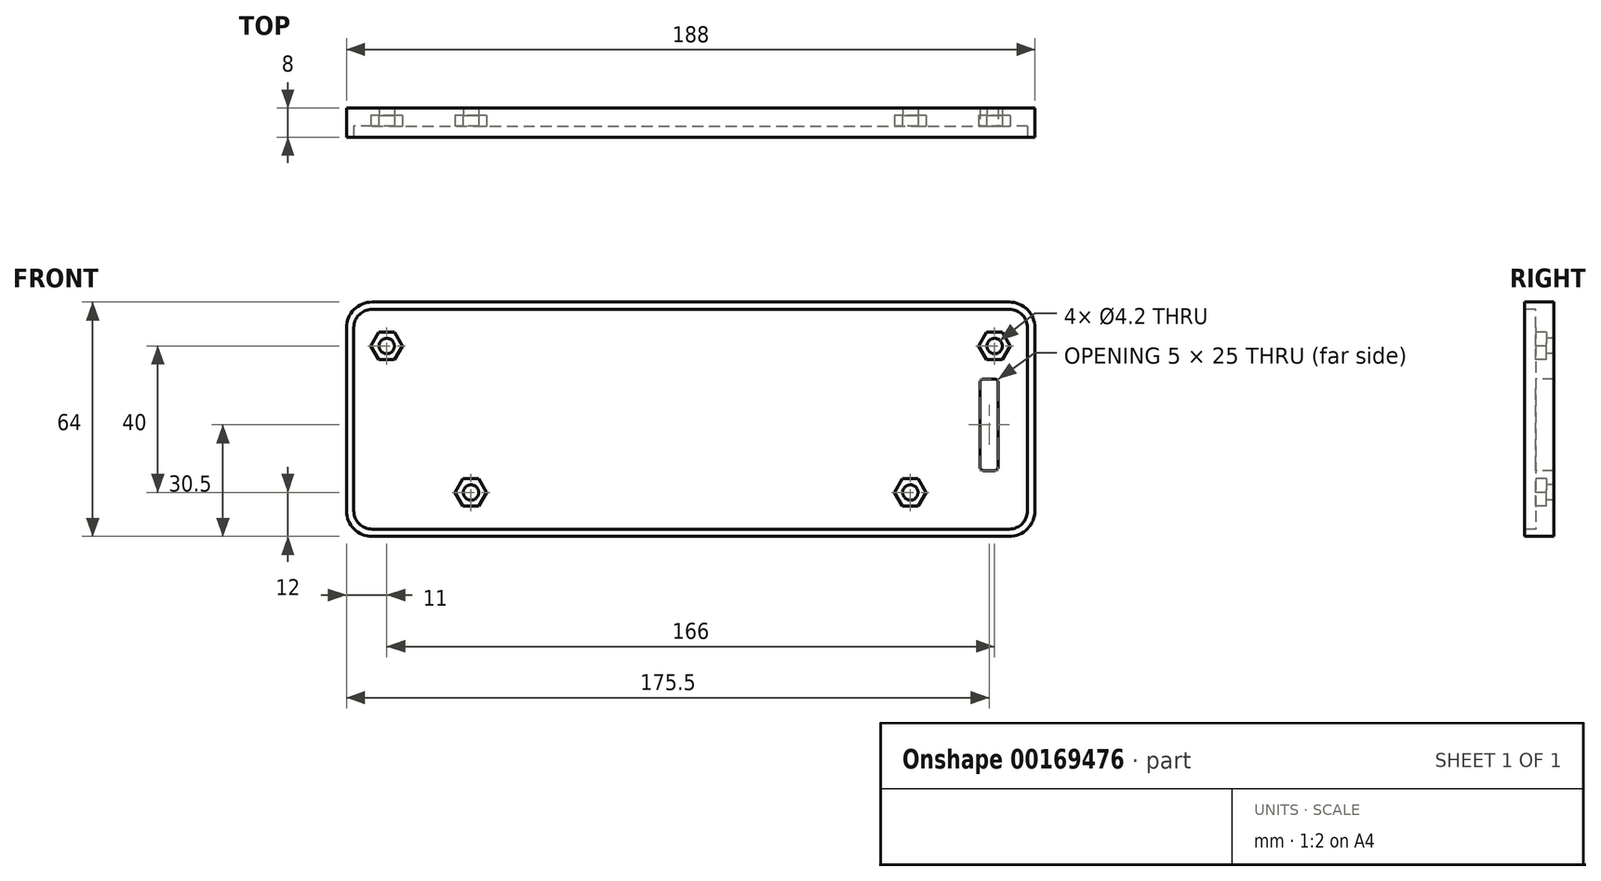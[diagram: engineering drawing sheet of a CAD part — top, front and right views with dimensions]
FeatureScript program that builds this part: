
annotation { "Feature Type Name" : "Feature", "Feature Type Description" : "" }
export const myFeature = defineFeature(function(context is Context, id is Id, definition is map)
    precondition{}
    {
        {
            var Q0;
            Q0=qCreatedBy(makeId("Front.planeOp"),FACE);
            var sketch = newSketch(context, id + "F0", { "sketchPlane" : qUnion([Q0])});
            skLineSegment(sketch, "E0.bottom", {"start": v(87, -32) * mm, "end": v(-87, -32) * mm});
            skLineSegment(sketch, "E0.top", {"start": v(87, 32) * mm, "end": v(-87, 32) * mm});
            skLineSegment(sketch, "E0.left", {"start": v(94, -25) * mm, "end": v(94, 25) * mm});
            skLineSegment(sketch, "E0.right", {"start": v(-94, -25) * mm, "end": v(-94, 25) * mm});
            skPoint(sketch, "E0.middle", {"position": v(0, 0) * mm});
            skPoint(sketch, "E1.visualSharp", {"position": v(-94, 32) * mm});
            skArc(sketch, "E1.filletArc", {"start": v(-87, 32) * mm, "mid": v(-91.95, 29.95) * mm, "end": v(-94, 25) * mm});
            skPoint(sketch, "E2.visualSharp", {"position": v(94, 32) * mm});
            skArc(sketch, "E2.filletArc", {"start": v(94, 25) * mm, "mid": v(91.95, 29.95) * mm, "end": v(87, 32) * mm});
            skPoint(sketch, "E3.visualSharp", {"position": v(94, -32) * mm});
            skArc(sketch, "E3.filletArc", {"start": v(87, -32) * mm, "mid": v(91.95, -29.95) * mm, "end": v(94, -25) * mm});
            skPoint(sketch, "E4.visualSharp", {"position": v(-94, -32) * mm});
            skArc(sketch, "E4.filletArc", {"start": v(-94, -25) * mm, "mid": v(-91.95, -29.95) * mm, "end": v(-87, -32) * mm});
            skSolve(sketch);
        }
        {
            var Q0;
            Q0 = qSketchRegion(id + "F0", true);
            extrude(context, id + "F1", {"entities" : qUnion([Q0]), "depth" : 8 * mm});
        }
        {
            var Q0;
            Q0=makeQuery(id+"F1.opExtrude","CAP_FACE",FACE,{"disambiguationData":[OSD([sQuery(id+"F0.wireOp",EDGE,"E0.bottom"),sQuery(id+"F0.wireOp",EDGE,"E0.top"),sQuery(id+"F0.wireOp",EDGE,"E0.left"),sQuery(id+"F0.wireOp",EDGE,"E0.right"),sQuery(id+"F0.wireOp",EDGE,"E1.filletArc"),sQuery(id+"F0.wireOp",EDGE,"E2.filletArc"),sQuery(id+"F0.wireOp",EDGE,"E3.filletArc"),sQuery(id+"F0.wireOp",EDGE,"E4.filletArc")])],"isStart":false});
            var sketch = newSketch(context, id + "F2", { "sketchPlane" : qUnion([Q0])});
            skLineSegment(sketch, "E5.bottom", {"start": v(-87, 30) * mm, "end": v(87, 30) * mm});
            skLineSegment(sketch, "E5.top", {"start": v(-87, -30) * mm, "end": v(87, -30) * mm});
            skLineSegment(sketch, "E5.left", {"start": v(-92, 25) * mm, "end": v(-92, -25) * mm});
            skLineSegment(sketch, "E5.right", {"start": v(92, 25) * mm, "end": v(92, -25) * mm});
            skPoint(sketch, "E6.visualSharp", {"position": v(-92, 30) * mm});
            skArc(sketch, "E6.filletArc", {"start": v(-87, 30) * mm, "mid": v(-90.54, 28.54) * mm, "end": v(-92, 25) * mm});
            skPoint(sketch, "E7.visualSharp", {"position": v(92, 30) * mm});
            skArc(sketch, "E7.filletArc", {"start": v(92, 25) * mm, "mid": v(90.54, 28.54) * mm, "end": v(87, 30) * mm});
            skPoint(sketch, "E8.visualSharp", {"position": v(92, -30) * mm});
            skArc(sketch, "E8.filletArc", {"start": v(87, -30) * mm, "mid": v(90.54, -28.54) * mm, "end": v(92, -25) * mm});
            skPoint(sketch, "E9.visualSharp", {"position": v(-92, -30) * mm});
            skArc(sketch, "E9.filletArc", {"start": v(-92, -25) * mm, "mid": v(-90.54, -28.54) * mm, "end": v(-87, -30) * mm});
            skSolve(sketch);
        }
        {
            var Q0;
            Q0 = qSketchRegion(id + "F2", true);
            extrude(context, id + "F3", {"entities" : qUnion([Q0]), "operationType" : NewBodyOperationType.REMOVE, "oppositeDirection" : true, "depth" : 3 * mm});
        }
        {
            var Q0;
            Q0=makeQuery(id+"F0.imprint","IMPRINT",FACE,{"disambiguationData":[TD([[makeQuery(id+"F0.imprint","IMPRINT",EDGE,{"derivedFrom":sQuery(id+"F0.wireOp",EDGE,"E0.bottom")}),-1.0]])]});
            var sketch = newSketch(context, id + "F4", { "sketchPlane" : qUnion([Q0])});
            skLineSegment(sketch, "E10.bottom", {"start": v(-87, 30) * mm, "end": v(87, 30) * mm});
            skLineSegment(sketch, "E10.top", {"start": v(-87, -30) * mm, "end": v(87, -30) * mm});
            skLineSegment(sketch, "E10.left", {"start": v(-92, 25) * mm, "end": v(-92, -25) * mm});
            skLineSegment(sketch, "E10.right", {"start": v(92, 25) * mm, "end": v(92, -25) * mm});
            skPoint(sketch, "E11.visualSharp", {"position": v(92, -30) * mm});
            skPoint(sketch, "E12.visualSharp", {"position": v(-92, -30) * mm});
            skPoint(sketch, "E13.visualSharp", {"position": v(-92, 30) * mm});
            skPoint(sketch, "E14.visualSharp", {"position": v(92, 30) * mm});
            skArc(sketch, "E15.filletArc", {"start": v(-87, 30) * mm, "mid": v(-90.54, 28.54) * mm, "end": v(-92, 25) * mm});
            skArc(sketch, "E16.filletArc", {"start": v(-92, -25) * mm, "mid": v(-90.54, -28.54) * mm, "end": v(-87, -30) * mm});
            skArc(sketch, "E17.filletArc", {"start": v(92, 25) * mm, "mid": v(90.54, 28.54) * mm, "end": v(87, 30) * mm});
            skArc(sketch, "E18.filletArc", {"start": v(87, -30) * mm, "mid": v(90.54, -28.54) * mm, "end": v(92, -25) * mm});
            skSolve(sketch);
        }
        {
            var Q0;
            Q0=makeQuery(id+"F3.boolean.opBoolean","COPY",FACE,{"derivedFrom":makeQuery(id+"F3.opExtrude","CAP_FACE",FACE,{"disambiguationData":[OSD([sQuery(id+"F2.wireOp",EDGE,"E5.bottom"),sQuery(id+"F2.wireOp",EDGE,"E5.top"),sQuery(id+"F2.wireOp",EDGE,"E5.left"),sQuery(id+"F2.wireOp",EDGE,"E5.right"),sQuery(id+"F2.wireOp",EDGE,"E6.filletArc"),sQuery(id+"F2.wireOp",EDGE,"E7.filletArc"),sQuery(id+"F2.wireOp",EDGE,"E8.filletArc"),sQuery(id+"F2.wireOp",EDGE,"E9.filletArc")])],"isStart":false})});
            var sketch = newSketch(context, id + "F5", { "sketchPlane" : qUnion([Q0])});
            skLineSegment(sketch, "E19", {"start": v(-92, 0) * mm, "end": v(92, 0) * mm, "construction": true});
            skLineSegment(sketch, "E20", {"start": v(0, 30) * mm, "end": v(0, -30) * mm, "construction": true});
            skSolve(sketch);
        }
        {
            var Q0;
            Q0=makeQuery(id+"F5.imprint","IMPRINT",FACE,{"disambiguationData":[TD([[makeQuery(id+"F5.imprint","IMPRINT",EDGE,{"derivedFrom":makeQuery(id+"F3.boolean.opBoolean","COPY",EDGE,{"derivedFrom":makeQuery(id+"F3.opExtrude","CAP_EDGE",EDGE,{"disambiguationData":[OSD([sQuery(id+"F2.wireOp",EDGE,"E5.bottom")])],"isStart":false})})}),-1.0]])]});
            var sketch = newSketch(context, id + "F6", { "sketchPlane" : qUnion([Q0])});
            skCircle(sketch, "E21.cCircle", {"center": v(60, -20) * mm, "radius": 3.75 * mm, "construction": true});
            skLineSegment(sketch, "E21.0", {"start": v(57.83, -23.75) * mm, "end": v(55.67, -20) * mm});
            skLineSegment(sketch, "E21.1", {"start": v(55.67, -20) * mm, "end": v(57.83, -16.25) * mm});
            skLineSegment(sketch, "E21.2", {"start": v(57.83, -16.25) * mm, "end": v(62.17, -16.25) * mm});
            skLineSegment(sketch, "E21.3", {"start": v(62.17, -16.25) * mm, "end": v(64.33, -20) * mm});
            skLineSegment(sketch, "E21.4", {"start": v(64.33, -20) * mm, "end": v(62.17, -23.75) * mm});
            skLineSegment(sketch, "E21.5", {"start": v(62.17, -23.75) * mm, "end": v(57.83, -23.75) * mm});
            skPoint(sketch, "E21.0.midPoint", {"position": v(56.75, -21.88) * mm});
            skCircle(sketch, "E22.cCircle", {"center": v(83, 20) * mm, "radius": 3.75 * mm, "construction": true});
            skLineSegment(sketch, "E22.0", {"start": v(80.83, 16.25) * mm, "end": v(78.67, 20) * mm});
            skLineSegment(sketch, "E22.1", {"start": v(78.67, 20) * mm, "end": v(80.83, 23.75) * mm});
            skLineSegment(sketch, "E22.2", {"start": v(80.83, 23.75) * mm, "end": v(85.17, 23.75) * mm});
            skLineSegment(sketch, "E22.3", {"start": v(85.17, 23.75) * mm, "end": v(87.33, 20) * mm});
            skLineSegment(sketch, "E22.4", {"start": v(87.33, 20) * mm, "end": v(85.17, 16.25) * mm});
            skLineSegment(sketch, "E22.5", {"start": v(85.17, 16.25) * mm, "end": v(80.83, 16.25) * mm});
            skPoint(sketch, "E22.0.midPoint", {"position": v(79.75, 18.12) * mm});
            skCircle(sketch, "E23.cCircle", {"center": v(-60, -20) * mm, "radius": 3.75 * mm, "construction": true});
            skLineSegment(sketch, "E23.0", {"start": v(-62.17, -23.75) * mm, "end": v(-64.33, -20) * mm});
            skLineSegment(sketch, "E23.1", {"start": v(-64.33, -20) * mm, "end": v(-62.17, -16.25) * mm});
            skLineSegment(sketch, "E23.2", {"start": v(-62.17, -16.25) * mm, "end": v(-57.83, -16.25) * mm});
            skLineSegment(sketch, "E23.3", {"start": v(-57.83, -16.25) * mm, "end": v(-55.67, -20) * mm});
            skLineSegment(sketch, "E23.4", {"start": v(-55.67, -20) * mm, "end": v(-57.83, -23.75) * mm});
            skLineSegment(sketch, "E23.5", {"start": v(-57.83, -23.75) * mm, "end": v(-62.17, -23.75) * mm});
            skPoint(sketch, "E23.0.midPoint", {"position": v(-63.75, -20) * mm});
            skCircle(sketch, "E24.cCircle", {"center": v(-83, 20) * mm, "radius": 3.75 * mm, "construction": true});
            skLineSegment(sketch, "E24.0", {"start": v(-85.17, 16.25) * mm, "end": v(-87.33, 20) * mm});
            skLineSegment(sketch, "E24.1", {"start": v(-87.33, 20) * mm, "end": v(-85.17, 23.75) * mm});
            skLineSegment(sketch, "E24.2", {"start": v(-85.17, 23.75) * mm, "end": v(-80.83, 23.75) * mm});
            skLineSegment(sketch, "E24.3", {"start": v(-80.83, 23.75) * mm, "end": v(-78.67, 20) * mm});
            skLineSegment(sketch, "E24.4", {"start": v(-78.67, 20) * mm, "end": v(-80.83, 16.25) * mm});
            skLineSegment(sketch, "E24.5", {"start": v(-80.83, 16.25) * mm, "end": v(-85.17, 16.25) * mm});
            skPoint(sketch, "E24.0.midPoint", {"position": v(-86.25, 18.13) * mm});
            skSolve(sketch);
        }
        {
            var Q0;
            Q0 = qSketchRegion(id + "F6", true);
            extrude(context, id + "F7", {"entities" : qUnion([Q0]), "operationType" : NewBodyOperationType.REMOVE, "oppositeDirection" : true, "depth" : 3 * mm});
        }
        {
            var Q0;
            Q0=makeQuery(id+"F5.imprint","IMPRINT",FACE,{"disambiguationData":[TD([[makeQuery(id+"F5.imprint","IMPRINT",EDGE,{"derivedFrom":makeQuery(id+"F3.boolean.opBoolean","COPY",EDGE,{"derivedFrom":makeQuery(id+"F3.opExtrude","CAP_EDGE",EDGE,{"disambiguationData":[OSD([sQuery(id+"F2.wireOp",EDGE,"E5.bottom")])],"isStart":false})})}),-1.0]])]});
            var sketch = newSketch(context, id + "F8", { "sketchPlane" : qUnion([Q0])});
            skCircle(sketch, "E25", {"center": v(-83, 20) * mm, "radius": 2.1 * mm});
            skCircle(sketch, "E26", {"center": v(-60, -20) * mm, "radius": 2.1 * mm});
            skCircle(sketch, "E27", {"center": v(83, 20) * mm, "radius": 2.1 * mm});
            skCircle(sketch, "E28", {"center": v(60, -20) * mm, "radius": 2.1 * mm});
            skSolve(sketch);
        }
        {
            var Q0;
            Q0 = qSketchRegion(id + "F8", true);
            var Q1;
            Q1=makeQuery(id+"F1.opExtrude","CAP_FACE",FACE,{"disambiguationData":[OSD([sQuery(id+"F0.wireOp",EDGE,"E0.bottom"),sQuery(id+"F0.wireOp",EDGE,"E0.top"),sQuery(id+"F0.wireOp",EDGE,"E0.left"),sQuery(id+"F0.wireOp",EDGE,"E0.right"),sQuery(id+"F0.wireOp",EDGE,"E1.filletArc"),sQuery(id+"F0.wireOp",EDGE,"E2.filletArc"),sQuery(id+"F0.wireOp",EDGE,"E3.filletArc"),sQuery(id+"F0.wireOp",EDGE,"E4.filletArc")])],"isStart":true});
            extrude(context, id + "F9", {"entities" : qUnion([Q0]), "operationType" : NewBodyOperationType.REMOVE, "endBound" : BoundingType.UP_TO_SURFACE, "oppositeDirection" : true, "endBoundEntityFace" : qUnion([Q1]), "depth" : 25 * mm});
        }
        {
            var Q0;
            Q0=makeQuery(id+"F3.boolean.opBoolean","COPY",FACE,{"derivedFrom":makeQuery(id+"F3.opExtrude","SWEPT_FACE",FACE,{"disambiguationData":[OSD([sQuery(id+"F2.wireOp",EDGE,"E5.left")])]})});
            var sketch = newSketch(context, id + "F10", { "sketchPlane" : qUnion([Q0])});
            skLineSegment(sketch, "E29.bottom", {"start": v(-6.2, -10) * mm, "end": v(-5, -10) * mm});
            skLineSegment(sketch, "E29.top", {"start": v(-6.2, -21) * mm, "end": v(-5, -21) * mm});
            skLineSegment(sketch, "E29.left", {"start": v(-6.2, -10) * mm, "end": v(-6.2, -21) * mm});
            skLineSegment(sketch, "E29.right", {"start": v(-5, -10) * mm, "end": v(-5, -21) * mm});
            skLineSegment(sketch, "E30.bottom", {"start": v(-6.2, 21) * mm, "end": v(-5, 21) * mm});
            skLineSegment(sketch, "E30.top", {"start": v(-6.2, 10) * mm, "end": v(-5, 10) * mm});
            skLineSegment(sketch, "E30.left", {"start": v(-6.2, 21) * mm, "end": v(-6.2, 10) * mm});
            skLineSegment(sketch, "E30.right", {"start": v(-5, 21) * mm, "end": v(-5, 10) * mm});
            skSolve(sketch);
        }
        {
            var Q0;
            Q0=makeQuery(id+"F3.boolean.opBoolean","COPY",FACE,{"derivedFrom":makeQuery(id+"F3.opExtrude","SWEPT_FACE",FACE,{"disambiguationData":[OSD([sQuery(id+"F2.wireOp",EDGE,"E5.right")])]})});
            var sketch = newSketch(context, id + "F11", { "sketchPlane" : qUnion([Q0])});
            skLineSegment(sketch, "E31.bottom", {"start": v(5, 21) * mm, "end": v(6.2, 21) * mm});
            skLineSegment(sketch, "E31.top", {"start": v(5, 10) * mm, "end": v(6.2, 10) * mm});
            skLineSegment(sketch, "E31.left", {"start": v(5, 21) * mm, "end": v(5, 10) * mm});
            skLineSegment(sketch, "E31.right", {"start": v(6.2, 21) * mm, "end": v(6.2, 10) * mm});
            skLineSegment(sketch, "E32.bottom", {"start": v(5, -21) * mm, "end": v(6.2, -21) * mm});
            skLineSegment(sketch, "E32.top", {"start": v(5, -10) * mm, "end": v(6.2, -10) * mm});
            skLineSegment(sketch, "E32.left", {"start": v(5, -10) * mm, "end": v(5, -21) * mm});
            skLineSegment(sketch, "E32.right", {"start": v(6.2, -10) * mm, "end": v(6.2, -21) * mm});
            skSolve(sketch);
        }
        {
            var Q0;
            Q0=makeQuery(id+"FXRFE9z9mOGoDKD_1.boolean.opBoolean","MERGE",FACE,{"derivedFrom":[makeQuery(id+"FHSEXAi1wgHX63n_1.boolean.opBoolean","MERGE",FACE,{"derivedFrom":[makeQuery(id+"FVbHBnZoGS1GzSc_1.boolean.opBoolean","MERGE",FACE,{"derivedFrom":[makeQuery(id+"F3.boolean.opBoolean","COPY",FACE,{"derivedFrom":makeQuery(id+"F3.opExtrude","CAP_FACE",FACE,{"disambiguationData":[OSD([sQuery(id+"F2.wireOp",EDGE,"E5.bottom"),sQuery(id+"F2.wireOp",EDGE,"E5.top"),sQuery(id+"F2.wireOp",EDGE,"E5.left"),sQuery(id+"F2.wireOp",EDGE,"E5.right"),sQuery(id+"F2.wireOp",EDGE,"E6.filletArc"),sQuery(id+"F2.wireOp",EDGE,"E7.filletArc"),sQuery(id+"F2.wireOp",EDGE,"E8.filletArc"),sQuery(id+"F2.wireOp",EDGE,"E9.filletArc")])],"isStart":false})}),makeQuery(id+"FVbHBnZoGS1GzSc_1.opExtrude","SWEPT_FACE",FACE,{"disambiguationData":[OSD([sQuery(id+"F10.wireOp",EDGE,"f3jfxRYR-zEYV-4sXy-QslR-nipfOOar7KBW")])]})]}),makeQuery(id+"FHSEXAi1wgHX63n_1.opExtrude","SWEPT_FACE",FACE,{"disambiguationData":[OSD([sQuery(id+"F11.wireOp",EDGE,"W6rOKNuU-GTvi-akX3-pjKq-6DrbPIyYzJpk"),sQuery(id+"F11.wireOp",EDGE,"2wJdlAmh-kTGb-LktZ-zVvI-ko3Y32ltAbLw")])]})]}),makeQuery(id+"FXRFE9z9mOGoDKD_1.opExtrude","SWEPT_FACE",FACE,{"disambiguationData":[OSD([sQuery(id+"FBFUB2NdTQuH0OG_1.wireOp",EDGE,"6aijx3dq-d6Lm-KUiO-0isF-x3RtKitpbzHq.left")])]}),makeQuery(id+"FXRFE9z9mOGoDKD_1.opExtrude","SWEPT_FACE",FACE,{"disambiguationData":[OSD([sQuery(id+"FBFUB2NdTQuH0OG_1.wireOp",EDGE,"qvhCP28Z-sYGW-Vd2a-yzUL-4GDnQVefEPHR.left")])]})]});
            var sketch = newSketch(context, id + "F12", { "sketchPlane" : qUnion([Q0])});
            skLineSegment(sketch, "E33.bottom", {"start": v(80, -14) * mm, "end": v(83, -14) * mm});
            skLineSegment(sketch, "E33.top", {"start": v(80, 11) * mm, "end": v(83, 11) * mm});
            skLineSegment(sketch, "E33.left", {"start": v(79, -13) * mm, "end": v(79, 10) * mm});
            skLineSegment(sketch, "E33.right", {"start": v(84, -13) * mm, "end": v(84, 10) * mm});
            skPoint(sketch, "E34.visualSharp", {"position": v(79, 11) * mm});
            skArc(sketch, "E34.filletArc", {"start": v(80, 11) * mm, "mid": v(79.3, 10.7) * mm, "end": v(79, 10) * mm});
            skPoint(sketch, "E35.visualSharp", {"position": v(84, 11) * mm});
            skArc(sketch, "E35.filletArc", {"start": v(84, 10) * mm, "mid": v(83.7, 10.7) * mm, "end": v(83, 11) * mm});
            skPoint(sketch, "E36.visualSharp", {"position": v(84, -14) * mm});
            skArc(sketch, "E36.filletArc", {"start": v(83, -14) * mm, "mid": v(83.7, -13.7) * mm, "end": v(84, -13) * mm});
            skPoint(sketch, "E37.visualSharp", {"position": v(79, -14) * mm});
            skArc(sketch, "E37.filletArc", {"start": v(79, -13) * mm, "mid": v(79.3, -13.7) * mm, "end": v(80, -14) * mm});
            skSolve(sketch);
        }
        {
            var Q0;
            Q0 = qSketchRegion(id + "F12", true);
            extrude(context, id + "F13", {"entities" : qUnion([Q0]), "operationType" : NewBodyOperationType.REMOVE, "oppositeDirection" : true, "depth" : 25 * mm});
        }
    });
